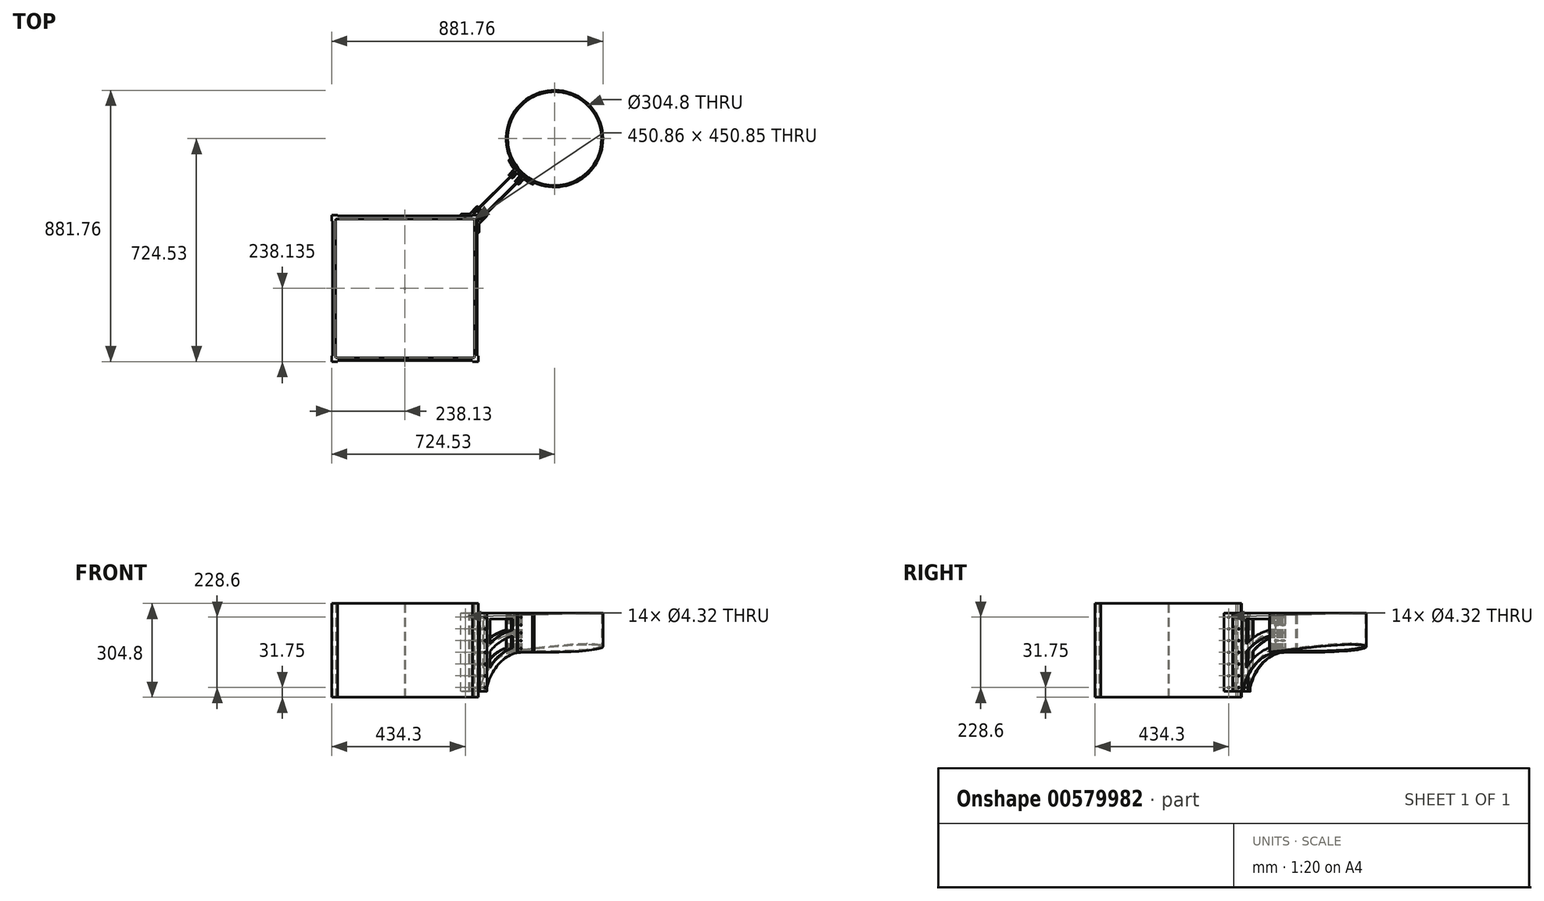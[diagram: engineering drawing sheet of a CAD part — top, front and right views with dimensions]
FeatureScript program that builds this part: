
annotation { "Feature Type Name" : "Feature", "Feature Type Description" : "" }
export const myFeature = defineFeature(function(context is Context, id is Id, definition is map)
    precondition{}
    {
        {
            var Q0;
            Q0=qCreatedBy(makeId("Top.planeOp"),FACE);
            var sketch = newSketch(context, id + "F0", { "sketchPlane" : qUnion([Q0])});
            skLineSegment(sketch, "E0.bottom", {"start": v(234.95, -234.95) * mm, "end": v(-234.95, -234.95) * mm});
            skLineSegment(sketch, "E0.top", {"start": v(234.95, 234.95) * mm, "end": v(-234.95, 234.95) * mm});
            skLineSegment(sketch, "E0.left", {"start": v(234.95, -234.95) * mm, "end": v(234.95, 234.95) * mm});
            skLineSegment(sketch, "E0.right", {"start": v(-234.95, -234.95) * mm, "end": v(-234.95, 234.95) * mm});
            skPoint(sketch, "E0.middle", {"position": v(0, 0) * mm});
            skLineSegment(sketch, "E1", {"start": v(0, 0) * mm, "end": v(234.95, 234.95) * mm});
            skLineSegment(sketch, "E2", {"start": v(234.95, 234.95) * mm, "end": v(486.4, 486.4) * mm});
            skCircle(sketch, "E3", {"center": v(486.4, 486.4) * mm, "radius": 152.4 * mm});
            skCircle(sketch, "E4", {"center": v(486.4, 486.4) * mm, "radius": 157.23 * mm});
            skLineSegment(sketch, "E5", {"start": v(-234.95, 234.95) * mm, "end": v(-234.95, 238.13) * mm});
            skLineSegment(sketch, "E6", {"start": v(-234.95, 238.13) * mm, "end": v(-238.13, 238.13) * mm});
            skLineSegment(sketch, "E7", {"start": v(-238.13, 238.13) * mm, "end": v(-238.13, 219.08) * mm});
            skLineSegment(sketch, "E8", {"start": v(-238.13, 219.08) * mm, "end": v(-234.95, 219.08) * mm});
            skLineSegment(sketch, "E9", {"start": v(-238.13, 238.13) * mm, "end": v(-219.08, 238.13) * mm});
            skLineSegment(sketch, "E10", {"start": v(-219.08, 238.13) * mm, "end": v(-219.08, 234.95) * mm});
            skLineSegment(sketch, "E11.1.0", {"start": v(-238.13, -238.13) * mm, "end": v(-219.08, -238.13) * mm});
            skLineSegment(sketch, "E11.1.1", {"start": v(-238.13, -238.13) * mm, "end": v(-238.13, -219.08) * mm});
            skLineSegment(sketch, "E11.1.2", {"start": v(-238.13, -219.08) * mm, "end": v(-234.95, -219.08) * mm});
            skLineSegment(sketch, "E11.1.3", {"start": v(-219.08, -238.13) * mm, "end": v(-219.08, -234.95) * mm});
            skLineSegment(sketch, "E11.1.4", {"start": v(-238.13, -234.95) * mm, "end": v(-238.13, -238.13) * mm});
            skLineSegment(sketch, "E11.1.5", {"start": v(-234.95, -234.95) * mm, "end": v(-238.13, -234.95) * mm});
            skLineSegment(sketch, "E11.2.0", {"start": v(238.13, -238.13) * mm, "end": v(238.13, -219.08) * mm});
            skLineSegment(sketch, "E11.2.1", {"start": v(238.13, -238.13) * mm, "end": v(219.08, -238.13) * mm});
            skLineSegment(sketch, "E11.2.2", {"start": v(219.08, -238.13) * mm, "end": v(219.08, -234.95) * mm});
            skLineSegment(sketch, "E11.2.3", {"start": v(238.13, -219.08) * mm, "end": v(234.95, -219.08) * mm});
            skLineSegment(sketch, "E11.2.4", {"start": v(234.95, -238.13) * mm, "end": v(238.13, -238.13) * mm});
            skLineSegment(sketch, "E11.2.5", {"start": v(234.95, -234.95) * mm, "end": v(234.95, -238.13) * mm});
            skLineSegment(sketch, "E11.3.0", {"start": v(238.13, 238.13) * mm, "end": v(219.08, 238.13) * mm});
            skLineSegment(sketch, "E11.3.1", {"start": v(238.13, 238.13) * mm, "end": v(238.13, 219.08) * mm});
            skLineSegment(sketch, "E11.3.2", {"start": v(238.13, 219.08) * mm, "end": v(234.95, 219.08) * mm});
            skLineSegment(sketch, "E11.3.3", {"start": v(219.08, 238.13) * mm, "end": v(219.08, 234.95) * mm});
            skLineSegment(sketch, "E11.3.4", {"start": v(238.13, 234.95) * mm, "end": v(238.13, 238.13) * mm});
            skLineSegment(sketch, "E11.3.5", {"start": v(234.95, 234.95) * mm, "end": v(238.13, 234.95) * mm});
            skLineSegment(sketch, "E12.0", {"start": v(-225.42, -225.42) * mm, "end": v(-225.43, 225.43) * mm});
            skLineSegment(sketch, "E12.1", {"start": v(225.43, -225.42) * mm, "end": v(-225.42, -225.42) * mm});
            skLineSegment(sketch, "E12.2", {"start": v(225.43, -225.42) * mm, "end": v(225.42, 225.43) * mm});
            skLineSegment(sketch, "E12.3", {"start": v(225.42, 225.43) * mm, "end": v(-225.43, 225.43) * mm});
            skSolve(sketch);
        }
        {
            var Q0;
            Q0=makeQuery(id+"F0.imprint","IMPRINT",FACE,{"disambiguationData":[TD([[makeQuery(id+"F0.imprint","IMPRINT",EDGE,{"derivedFrom":sQuery(id+"F0.wireOp",EDGE,"E3")}),-1.0]])]});
            extrude(context, id + "F1", {"entities" : qUnion([Q0]), "depth" : 304.8 * mm, "offsetDistance" : 25.4 * mm});
        }
        {
            var Q0;
            Q0=makeQuery(id+"F0.imprint","IMPRINT",FACE,{"disambiguationData":[TD([[makeQuery(id+"F0.imprint","IMPRINT",EDGE,{"derivedFrom":sQuery(id+"F0.wireOp",EDGE,"E12.0")}),1.0]])]});
            var Q1;
            Q1=makeQuery(id+"F0.imprint","IMPRINT",FACE,{"disambiguationData":[TD([[makeQuery(id+"F0.imprint","IMPRINT",EDGE,{"derivedFrom":sQuery(id+"F0.wireOp",EDGE,"E11.3.1")}),-1.0]])]});
            var Q2;
            {var subQ4=sQuery(id+"F0.wireOp",EDGE,"E11.3.0");Q2=makeQuery(id+"F0.imprint","IMPRINT",FACE,{"disambiguationData":[TD([[makeQuery(id+"F0.imprint","IMPRINT",EDGE,{"derivedFrom":subQ4}),1.0]])]});}
            var Q3;
            Q3=makeQuery(id+"F0.imprint","IMPRINT",FACE,{"disambiguationData":[TD([[makeQuery(id+"F0.imprint","IMPRINT",EDGE,{"derivedFrom":sQuery(id+"F0.wireOp",EDGE,"E11.2.0")}),1.0]])]});
            var Q4;
            {var subQ1=sQuery(id+"F0.wireOp",EDGE,"E5");Q4=makeQuery(id+"F0.imprint","IMPRINT",FACE,{"disambiguationData":[TD([[makeQuery(id+"F0.imprint","IMPRINT",EDGE,{"derivedFrom":subQ1}),1.0]])]});}
            var Q5;
            Q5=makeQuery(id+"F0.imprint","IMPRINT",FACE,{"disambiguationData":[TD([[makeQuery(id+"F0.imprint","IMPRINT",EDGE,{"derivedFrom":sQuery(id+"F0.wireOp",EDGE,"E11.2.1")}),-1.0]])]});
            var Q6;
            {var subQ0=sQuery(id+"F0.wireOp",EDGE,"E5");Q6=makeQuery(id+"F0.imprint","IMPRINT",FACE,{"disambiguationData":[TD([[makeQuery(id+"F0.imprint","IMPRINT",EDGE,{"derivedFrom":subQ0}),-1.0]])]});}
            var Q7;
            Q7=makeQuery(id+"F0.imprint","IMPRINT",FACE,{"disambiguationData":[TD([[makeQuery(id+"F0.imprint","IMPRINT",EDGE,{"derivedFrom":sQuery(id+"F0.wireOp",EDGE,"E11.1.0")}),1.0]])]});
            var Q8;
            Q8=makeQuery(id+"F0.imprint","IMPRINT",FACE,{"disambiguationData":[TD([[makeQuery(id+"F0.imprint","IMPRINT",EDGE,{"derivedFrom":sQuery(id+"F0.wireOp",EDGE,"E11.1.1")}),-1.0]])]});
            var Q9;
            {var subQ2=sQuery(id+"F0.wireOp",EDGE,"E11.3.4");Q9=makeQuery(id+"F0.imprint","IMPRINT",FACE,{"disambiguationData":[TD([[makeQuery(id+"F0.imprint","IMPRINT",EDGE,{"derivedFrom":subQ2}),1.0]])]});}
            extrude(context, id + "F2", {"entities" : qUnion([Q0, Q1, Q2, Q3, Q4, Q5, Q6, Q7, Q8, Q9]), "depth" : 304.8 * mm, "offsetDistance" : 25.4 * mm});
        }
        {
            var Q0;
            Q0=makeQuery(id+"F1.opExtrude","CAP_FACE",FACE,{"disambiguationData":[OSD([sQuery(id+"F0.wireOp",EDGE,"E3"),sQuery(id+"F0.wireOp",EDGE,"E4")])],"isStart":false});
            var sketch = newSketch(context, id + "F3", { "sketchPlane" : qUnion([Q0])});
            skCircle(sketch, "E13", {"center": v(486.4, 486.4) * mm, "radius": 157.23 * mm});
            skArc(sketch, "E14", {"start": v(366.99, 372.3) * mm, "mid": v(369.6, 369.6) * mm, "end": v(372.3, 366.99) * mm});
            skLineSegment(sketch, "E15", {"start": v(486.4, 486.4) * mm, "end": v(643.62, 486.4) * mm});
            skLineSegment(sketch, "E16", {"start": v(643.62, 486.4) * mm, "end": v(645.21, 486.4) * mm});
            skCircle(sketch, "E17", {"center": v(486.4, 486.4) * mm, "radius": 158.81 * mm});
            skLineSegment(sketch, "E18", {"start": v(369.6, 369.6) * mm, "end": v(244.47, 244.48) * mm});
            skLineSegment(sketch, "E19", {"start": v(486.4, 486.4) * mm, "end": v(477.42, 495.38) * mm});
            skLineSegment(sketch, "E20", {"start": v(360.97, 378.93) * mm, "end": v(345.53, 363.49) * mm});
            skLineSegment(sketch, "E21", {"start": v(477.42, 495.38) * mm, "end": v(475.17, 497.62) * mm});
            skLineSegment(sketch, "E22", {"start": v(358.92, 381.37) * mm, "end": v(343.28, 365.73) * mm});
            skLineSegment(sketch, "E23", {"start": v(645.21, 486.4) * mm, "end": v(651.56, 486.4) * mm});
            skLineSegment(sketch, "E24", {"start": v(238.13, 238.13) * mm, "end": v(219.08, 238.13) * mm});
            skLineSegment(sketch, "E25", {"start": v(219.08, 238.13) * mm, "end": v(219.08, 234.95) * mm});
            skLineSegment(sketch, "E26", {"start": v(219.08, 234.95) * mm, "end": v(180.98, 234.95) * mm});
            skLineSegment(sketch, "E27", {"start": v(180.98, 234.95) * mm, "end": v(180.98, 238.76) * mm});
            skLineSegment(sketch, "E28", {"start": v(475.17, 497.62) * mm, "end": v(470.68, 502.11) * mm});
            skLineSegment(sketch, "E29", {"start": v(353.4, 384.83) * mm, "end": v(338.8, 370.22) * mm});
            skLineSegment(sketch, "E30", {"start": v(477.42, 495.38) * mm, "end": v(481.9, 490.89) * mm});
            skLineSegment(sketch, "E31", {"start": v(363.35, 372.33) * mm, "end": v(350.02, 359) * mm});
            skLineSegment(sketch, "E32", {"start": v(353.4, 384.83) * mm, "end": v(337, 368.43) * mm});
            skLineSegment(sketch, "E33", {"start": v(338.8, 366.63) * mm, "end": v(339.69, 365.73) * mm});
            skArc(sketch, "E34.trimOffspring", {"start": v(358.92, 381.37) * mm, "mid": v(359.94, 380.15) * mm, "end": v(360.97, 378.93) * mm});
            skLineSegment(sketch, "E35.trimOffspring", {"start": v(345.53, 359.9) * mm, "end": v(346.42, 359) * mm});
            skLineSegment(sketch, "E36", {"start": v(235.5, 244.48) * mm, "end": v(245.3, 254.29) * mm});
            skLineSegment(sketch, "E37", {"start": v(245.3, 257.88) * mm, "end": v(244.41, 258.78) * mm});
            skLineSegment(sketch, "E38.trimOffspring", {"start": v(234.08, 265.51) * mm, "end": v(210.61, 242.04) * mm});
            skLineSegment(sketch, "E39.trimOffspring", {"start": v(247.1, 256.09) * mm, "end": v(235.5, 244.47) * mm});
            skLineSegment(sketch, "E40", {"start": v(183.52, 241.3) * mm, "end": v(208.82, 241.3) * mm});
            skLineSegment(sketch, "E41", {"start": v(238.13, 244.48) * mm, "end": v(235.5, 244.48) * mm});
            skLineSegment(sketch, "E42", {"start": v(223.34, 241.3) * mm, "end": v(221.1, 243.55) * mm});
            skLineSegment(sketch, "E43.trimOffspring", {"start": v(238.57, 264.62) * mm, "end": v(237.68, 265.51) * mm});
            skLineSegment(sketch, "E44", {"start": v(486.4, 486.4) * mm, "end": v(339.03, 417.68) * mm});
            skPoint(sketch, "E45.visualSharp", {"position": v(354.96, 386.39) * mm});
            skArc(sketch, "E45.filletArc", {"start": v(353.4, 384.83) * mm, "mid": v(354.13, 386.44) * mm, "end": v(353.64, 388.14) * mm});
            skPoint(sketch, "E46.visualSharp", {"position": v(337, 368.43) * mm});
            skArc(sketch, "E46.filletArc", {"start": v(338.8, 370.22) * mm, "mid": v(338.05, 368.43) * mm, "end": v(338.8, 366.63) * mm});
            skPoint(sketch, "E47.visualSharp", {"position": v(348.22, 357.2) * mm});
            skArc(sketch, "E47.filletArc", {"start": v(346.42, 359) * mm, "mid": v(348.22, 358.25) * mm, "end": v(350.02, 359) * mm});
            skPoint(sketch, "E48.visualSharp", {"position": v(365.2, 374.19) * mm});
            skArc(sketch, "E48.filletArc", {"start": v(366.99, 372.3) * mm, "mid": v(365.18, 373.08) * mm, "end": v(363.35, 372.33) * mm});
            skPoint(sketch, "E49.visualSharp", {"position": v(235.88, 267.31) * mm});
            skArc(sketch, "E49.filletArc", {"start": v(237.68, 265.51) * mm, "mid": v(235.88, 266.26) * mm, "end": v(234.08, 265.51) * mm});
            skPoint(sketch, "E50.visualSharp", {"position": v(247.1, 256.09) * mm});
            skArc(sketch, "E50.filletArc", {"start": v(245.3, 254.29) * mm, "mid": v(246.05, 256.09) * mm, "end": v(245.3, 257.88) * mm});
            skPoint(sketch, "E51.visualSharp", {"position": v(209.87, 241.3) * mm});
            skArc(sketch, "E51.filletArc", {"start": v(208.82, 241.3) * mm, "mid": v(209.79, 241.5) * mm, "end": v(210.61, 242.04) * mm});
            skPoint(sketch, "E52.visualSharp", {"position": v(180.98, 241.3) * mm});
            skArc(sketch, "E52.filletArc", {"start": v(183.52, 241.3) * mm, "mid": v(181.72, 240.56) * mm, "end": v(180.98, 238.76) * mm});
            skLineSegment(sketch, "E53.trimOffspring", {"start": v(238.57, 261.02) * mm, "end": v(221.1, 243.55) * mm});
            skLineSegment(sketch, "E54.trimOffspring", {"start": v(240.82, 258.78) * mm, "end": v(223.34, 241.3) * mm});
            skPoint(sketch, "E55.visualSharp", {"position": v(341.49, 363.94) * mm});
            skArc(sketch, "E55.filletArc", {"start": v(339.69, 365.73) * mm, "mid": v(341.49, 364.99) * mm, "end": v(343.28, 365.73) * mm});
            skPoint(sketch, "E56.visualSharp", {"position": v(343.73, 361.7) * mm});
            skArc(sketch, "E56.filletArc", {"start": v(345.53, 363.49) * mm, "mid": v(344.78, 361.7) * mm, "end": v(345.53, 359.9) * mm});
            skPoint(sketch, "E57.visualSharp", {"position": v(240.37, 262.82) * mm});
            skArc(sketch, "E57.filletArc", {"start": v(238.57, 261.02) * mm, "mid": v(239.32, 262.82) * mm, "end": v(238.57, 264.62) * mm});
            skPoint(sketch, "E58.visualSharp", {"position": v(242.62, 260.58) * mm});
            skArc(sketch, "E58.filletArc", {"start": v(244.41, 258.78) * mm, "mid": v(242.62, 259.52) * mm, "end": v(240.82, 258.78) * mm});
            skLineSegment(sketch, "E59.MirrorCS", {"start": v(359.9, 345.53) * mm, "end": v(359, 346.42) * mm});
            skArc(sketch, "E60.MirrorCS", {"start": v(363.49, 345.53) * mm, "mid": v(361.7, 344.78) * mm, "end": v(359.9, 345.53) * mm});
            skLineSegment(sketch, "E61.MirrorCS", {"start": v(366.63, 338.8) * mm, "end": v(365.73, 339.69) * mm});
            skArc(sketch, "E62.MirrorCS", {"start": v(372.3, 366.99) * mm, "mid": v(373.08, 365.18) * mm, "end": v(372.33, 363.35) * mm});
            skArc(sketch, "E63.MirrorCS", {"start": v(384.83, 353.4) * mm, "mid": v(386.44, 354.13) * mm, "end": v(388.14, 353.64) * mm});
            skArc(sketch, "E64.MirrorCS", {"start": v(359, 346.42) * mm, "mid": v(358.25, 348.22) * mm, "end": v(359, 350.02) * mm});
            skArc(sketch, "E65.MirrorCS", {"start": v(365.73, 339.69) * mm, "mid": v(364.99, 341.49) * mm, "end": v(365.73, 343.28) * mm});
            skArc(sketch, "E66.MirrorCS", {"start": v(370.22, 338.8) * mm, "mid": v(368.43, 338.05) * mm, "end": v(366.63, 338.8) * mm});
            skArc(sketch, "E67.MirrorCS", {"start": v(381.37, 358.92) * mm, "mid": v(380.15, 359.94) * mm, "end": v(378.93, 360.97) * mm});
            skLineSegment(sketch, "E68.MirrorCS", {"start": v(384.83, 353.4) * mm, "end": v(368.43, 337) * mm});
            skPoint(sketch, "E69.MirrorP", {"position": v(386.39, 354.96) * mm});
            skPoint(sketch, "E70.MirrorP", {"position": v(363.94, 341.49) * mm});
            skPoint(sketch, "E71.MirrorP", {"position": v(368.43, 337) * mm});
            skPoint(sketch, "E72.MirrorP", {"position": v(361.7, 343.73) * mm});
            skPoint(sketch, "E73.MirrorP", {"position": v(374.19, 365.2) * mm});
            skPoint(sketch, "E74.MirrorP", {"position": v(357.2, 348.22) * mm});
            skLineSegment(sketch, "E75.MirrorCS", {"start": v(381.37, 358.92) * mm, "end": v(365.73, 343.28) * mm});
            skLineSegment(sketch, "E76.MirrorCS", {"start": v(372.33, 363.35) * mm, "end": v(359, 350.02) * mm});
            skLineSegment(sketch, "E77.MirrorCS", {"start": v(378.93, 360.97) * mm, "end": v(363.49, 345.53) * mm});
            skLineSegment(sketch, "E78.MirrorCS", {"start": v(384.83, 353.4) * mm, "end": v(370.22, 338.8) * mm});
            skLineSegment(sketch, "E79.MirrorCS", {"start": v(486.4, 486.4) * mm, "end": v(417.68, 339.03) * mm});
            skLineSegment(sketch, "E80.MirrorCS", {"start": v(238.13, 219.08) * mm, "end": v(234.95, 219.08) * mm});
            skArc(sketch, "E81.MirrorCS", {"start": v(258.78, 244.41) * mm, "mid": v(259.52, 242.62) * mm, "end": v(258.78, 240.82) * mm});
            skArc(sketch, "E82.MirrorCS", {"start": v(265.51, 237.68) * mm, "mid": v(266.26, 235.88) * mm, "end": v(265.51, 234.08) * mm});
            skArc(sketch, "E83.MirrorCS", {"start": v(254.29, 245.3) * mm, "mid": v(256.09, 246.05) * mm, "end": v(257.88, 245.3) * mm});
            skLineSegment(sketch, "E84.MirrorCS", {"start": v(264.62, 238.57) * mm, "end": v(265.51, 237.68) * mm});
            skArc(sketch, "E85.MirrorCS", {"start": v(241.3, 208.82) * mm, "mid": v(241.5, 209.79) * mm, "end": v(242.04, 210.61) * mm});
            skLineSegment(sketch, "E86.MirrorCS", {"start": v(244.47, 238.13) * mm, "end": v(244.47, 235.5) * mm});
            skArc(sketch, "E87.MirrorCS", {"start": v(261.02, 238.57) * mm, "mid": v(262.82, 239.32) * mm, "end": v(264.62, 238.57) * mm});
            skArc(sketch, "E88.MirrorCS", {"start": v(241.3, 183.52) * mm, "mid": v(240.56, 181.72) * mm, "end": v(238.76, 180.98) * mm});
            skLineSegment(sketch, "E89.MirrorCS", {"start": v(257.88, 245.3) * mm, "end": v(258.78, 244.41) * mm});
            skLineSegment(sketch, "E90.MirrorCS", {"start": v(241.3, 223.34) * mm, "end": v(243.55, 221.1) * mm});
            skLineSegment(sketch, "E91.MirrorCS", {"start": v(234.95, 180.98) * mm, "end": v(238.76, 180.98) * mm});
            skLineSegment(sketch, "E92.MirrorCS", {"start": v(244.47, 235.5) * mm, "end": v(254.29, 245.3) * mm});
            skLineSegment(sketch, "E93.MirrorCS", {"start": v(238.13, 238.13) * mm, "end": v(238.13, 219.08) * mm});
            skPoint(sketch, "E94.MirrorP", {"position": v(256.09, 247.1) * mm});
            skPoint(sketch, "E95.MirrorP", {"position": v(262.82, 240.37) * mm});
            skPoint(sketch, "E96.MirrorP", {"position": v(241.3, 209.87) * mm});
            skLineSegment(sketch, "E97.MirrorCS", {"start": v(265.51, 234.08) * mm, "end": v(242.04, 210.61) * mm});
            skPoint(sketch, "E98.MirrorP", {"position": v(260.58, 242.62) * mm});
            skLineSegment(sketch, "E99.MirrorCS", {"start": v(261.02, 238.57) * mm, "end": v(243.55, 221.1) * mm});
            skPoint(sketch, "E100.MirrorP", {"position": v(267.31, 235.88) * mm});
            skLineSegment(sketch, "E101.MirrorCS", {"start": v(258.78, 240.82) * mm, "end": v(241.3, 223.34) * mm});
            skPoint(sketch, "E102.MirrorP", {"position": v(241.3, 180.98) * mm});
            skLineSegment(sketch, "E103.MirrorCS", {"start": v(241.3, 183.52) * mm, "end": v(241.3, 208.82) * mm});
            skLineSegment(sketch, "E104.MirrorCS", {"start": v(256.09, 247.1) * mm, "end": v(244.47, 235.5) * mm});
            skLineSegment(sketch, "E105.MirrorCS", {"start": v(234.95, 219.08) * mm, "end": v(234.95, 180.98) * mm});
            skLineSegment(sketch, "E106", {"start": v(238.13, 244.48) * mm, "end": v(241.94, 244.48) * mm});
            skLineSegment(sketch, "E107", {"start": v(244.47, 241.94) * mm, "end": v(244.47, 238.13) * mm});
            skPoint(sketch, "E108.MirrorCS.start.orphan", {"position": v(238.12, 238.13) * mm});
            skPoint(sketch, "E109.visualSharp", {"position": v(244.47, 244.48) * mm});
            skArc(sketch, "E109.filletArc", {"start": v(244.47, 241.94) * mm, "mid": v(243.73, 243.73) * mm, "end": v(241.94, 244.48) * mm});
            skLineSegment(sketch, "E110.0", {"start": v(216.54, 238.13) * mm, "end": v(216.54, 234.95) * mm});
            skLineSegment(sketch, "E111.0", {"start": v(238.13, 216.53) * mm, "end": v(234.95, 216.53) * mm});
            skLineSegment(sketch, "E112", {"start": v(219.08, 238.13) * mm, "end": v(216.54, 238.13) * mm});
            skLineSegment(sketch, "E113", {"start": v(238.13, 216.53) * mm, "end": v(238.13, 219.08) * mm});
            skArc(sketch, "E114.trimOffspring", {"start": v(378.93, 360.97) * mm, "mid": v(380.15, 359.94) * mm, "end": v(381.37, 358.92) * mm});
            skArc(sketch, "E115.trimOffspring", {"start": v(388.14, 353.64) * mm, "mid": v(400.83, 345.12) * mm, "end": v(414.27, 337.82) * mm});
            skArc(sketch, "E116.trimOffspring", {"start": v(337.82, 414.27) * mm, "mid": v(345.12, 400.83) * mm, "end": v(353.64, 388.14) * mm});
            skPoint(sketch, "E117.visualSharp", {"position": v(336.7, 416.6) * mm});
            skArc(sketch, "E117.filletArc", {"start": v(339.03, 417.68) * mm, "mid": v(337.7, 416.23) * mm, "end": v(337.82, 414.27) * mm});
            skPoint(sketch, "E118.visualSharp", {"position": v(416.6, 336.7) * mm});
            skArc(sketch, "E118.filletArc", {"start": v(414.27, 337.82) * mm, "mid": v(416.23, 337.7) * mm, "end": v(417.68, 339.03) * mm});
            skSolve(sketch);
        }
        {
            var Q0;
            Q0=makeQuery(id+"F3.imprint","IMPRINT",FACE,{"disambiguationData":[TD([[makeQuery(id+"F3.imprint","IMPRINT",EDGE,{"derivedFrom":sQuery(id+"F3.wireOp",EDGE,"E20")}),1.0]])]});
            var Q1;
            Q1=makeQuery(id+"F3.imprint","IMPRINT",FACE,{"disambiguationData":[TD([[makeQuery(id+"F3.imprint","IMPRINT",EDGE,{"derivedFrom":sQuery(id+"F3.wireOp",EDGE,"E24")}),-1.0]])]});
            extrude(context, id + "F4", {"entities" : qUnion([Q0, Q1]), "oppositeDirection" : true, "depth" : 254 * mm, "offsetDistance" : 25.4 * mm});
        }
        {
            var Q0;
            Q0=makeQuery(id+"F4.opExtrude","SWEPT_FACE",FACE,{"disambiguationData":[OSD([sQuery(id+"F3.wireOp",EDGE,"E97.MirrorCS")])]});
            var sketch = newSketch(context, id + "F5", { "sketchPlane" : qUnion([Q0])});
            skLineSegment(sketch, "E119", {"start": v(538.63, 304.8) * mm, "end": v(538.63, 177.8) * mm});
            skLineSegment(sketch, "E120", {"start": v(538.63, 177.8) * mm, "end": v(487.83, 177.8) * mm});
            skLineSegment(sketch, "E121", {"start": v(487.83, 177.8) * mm, "end": v(487.83, -25.4) * mm});
            skLineSegment(sketch, "E122", {"start": v(487.83, -25.4) * mm, "end": v(564.03, -25.4) * mm});
            skLineSegment(sketch, "E123", {"start": v(564.03, -25.4) * mm, "end": v(564.03, 177.8) * mm});
            skLineSegment(sketch, "E124", {"start": v(564.03, 177.8) * mm, "end": v(538.63, 177.8) * mm});
            skSolve(sketch);
        }
        {
            var Q0;
            Q0=makeQuery(id+"F5.imprint","IMPRINT",FACE,{"disambiguationData":[TD([[makeQuery(id+"F5.imprint","IMPRINT",EDGE,{"derivedFrom":sQuery(id+"F5.wireOp",EDGE,"E120")}),1.0]])]});
            extrude(context, id + "F6", {"entities" : qUnion([Q0]), "operationType" : NewBodyOperationType.REMOVE, "endBound" : BoundingType.SYMMETRIC, "oppositeDirection" : true, "depth" : 254 * mm, "offsetDistance" : 25.4 * mm});
        }
        {
            var Q0;
            Q0=makeQuery(id+"F4.opExtrude","SWEPT_FACE",FACE,{"disambiguationData":[OSD([sQuery(id+"F3.wireOp",EDGE,"E42")])]});
            var Q1;
            Q1=makeQuery(id+"F4.opExtrude","SWEPT_FACE",FACE,{"disambiguationData":[OSD([sQuery(id+"F3.wireOp",EDGE,"E90.MirrorCS")])]});
            extrude(context, id + "F7", {"entities" : qUnion([Q0, Q1]), "depth" : 194.3 * mm, "offsetDistance" : 25.4 * mm});
        }
        {
            var Q0;
            Q0=makeQuery(id+"F7.opExtrude","SWEPT_FACE",FACE,{"disambiguationData":[OSD([sQuery(id+"F3.wireOp",EDGE,"E90.MirrorCS"),sQuery(id+"F3.wireOp",EDGE,"E99.MirrorCS")])]});
            var sketch = newSketch(context, id + "F8", { "sketchPlane" : qUnion([Q0])});
            skLineSegment(sketch, "E125", {"start": v(355.8, 50.8) * mm, "end": v(355.8, 37.36) * mm});
            skLineSegment(sketch, "E126", {"start": v(522.86, 177.8) * mm, "end": v(532.9, 177.8) * mm});
            skArc(sketch, "E127", {"start": v(522.86, 177.8) * mm, "mid": v(417.94, 142.44) * mm, "end": v(355.8, 50.8) * mm});
            skLineSegment(sketch, "E128", {"start": v(355.8, 37.36) * mm, "end": v(550.78, 37.36) * mm});
            skLineSegment(sketch, "E129", {"start": v(532.9, 177.8) * mm, "end": v(532.9, 37.36) * mm});
            skSolve(sketch);
        }
        {
            var Q0;
            Q0=qSketchRegion(id+"F8",true);
            extrude(context, id + "F9", {"entities" : qUnion([Q0]), "operationType" : NewBodyOperationType.REMOVE, "oppositeDirection" : true, "depth" : 127 * mm, "offsetDistance" : 25.4 * mm});
        }
        {
            var Q0;
            {var subQ0=sQuery(id+"F3.wireOp",EDGE,"E44");var subQ1=sQuery(id+"F3.wireOp",EDGE,"E13");var subQ2=makeQuery(id+"F3.imprint","INTERSECT",VERTEX,{"derivedFrom":[subQ1,subQ0]});Q0=makeQuery(id+"F3.imprint","IMPRINT",FACE,{"disambiguationData":[TD([[makeQuery(id+"F3.imprint","IMPRINT",EDGE,{"disambiguationData":[TD([[subQ2,-1.0]])],"derivedFrom":subQ1}),-1.0]])]});}
            extrude(context, id + "F10", {"entities" : qUnion([Q0]), "oppositeDirection" : true, "depth" : 127 * mm, "offsetDistance" : 25.4 * mm});
        }
        {
            var Q0;
            Q0=sQuery(id+"F3.wireOp",EDGE,"E18");
            cPlane(context, id + "F11", {"entities" : qUnion([Q0]), "cplaneType" : CPlaneType.LINE_ANGLE, "offset" : 25.4 * mm, "angle" : 90 * degree, "width" : 152.4 * mm, "height" : 152.4 * mm});
        }
        {
            var Q0;
            Q0=qCreatedBy(id+"F11.planeOp",FACE);
            var sketch = newSketch(context, id + "F12", { "sketchPlane" : qUnion([Q0])});
            skLineSegment(sketch, "E130", {"start": v(521.3, 304.8) * mm, "end": v(521.3, 275.68) * mm});
            skLineSegment(sketch, "E131", {"start": v(521.3, 304.8) * mm, "end": v(687.87, 304.8) * mm});
            skLineSegment(sketch, "E132", {"start": v(687.87, 304.8) * mm, "end": v(530.64, 304.8) * mm});
            skLineSegment(sketch, "E133", {"start": v(530.64, 304.8) * mm, "end": v(530.64, 177.8) * mm});
            skLineSegment(sketch, "E134", {"start": v(687.87, 304.8) * mm, "end": v(845.1, 304.8) * mm});
            skLineSegment(sketch, "E135", {"start": v(845.1, 304.8) * mm, "end": v(845.1, 203.2) * mm});
            skLineSegment(sketch, "E136", {"start": v(530.64, 177.8) * mm, "end": v(526.36, 177.8) * mm});
            skArc(sketch, "E137", {"start": v(530.64, 177.8) * mm, "mid": v(688.38, 184.16) * mm, "end": v(845.1, 203.2) * mm});
            skLineSegment(sketch, "E138", {"start": v(845.1, 203.2) * mm, "end": v(870.5, 203.2) * mm});
            skLineSegment(sketch, "E139", {"start": v(870.5, 203.2) * mm, "end": v(870.5, -50.8) * mm});
            skLineSegment(sketch, "E140", {"start": v(870.5, -50.8) * mm, "end": v(526.36, -50.8) * mm});
            skLineSegment(sketch, "E141", {"start": v(526.36, 177.8) * mm, "end": v(526.36, -50.8) * mm});
            skSolve(sketch);
        }
        {
            var Q0;
            Q0=makeQuery(id+"F12.imprint","IMPRINT",FACE,{"disambiguationData":[TD([[makeQuery(id+"F12.imprint","IMPRINT",EDGE,{"derivedFrom":sQuery(id+"F12.wireOp",EDGE,"E136")}),1.0]])]});
            extrude(context, id + "F13", {"entities" : qUnion([Q0]), "operationType" : NewBodyOperationType.REMOVE, "endBound" : BoundingType.SYMMETRIC, "oppositeDirection" : true, "depth" : 381 * mm, "offsetDistance" : 25.4 * mm});
        }
        {
            var Q0;
            Q0=qCreatedBy(makeId("Top.planeOp"),FACE);
            var sketch = newSketch(context, id + "F14", { "sketchPlane" : qUnion([Q0])});
            skCircle(sketch, "E142", {"center": v(0, 0) * mm, "radius": 1.27 * mm});
            skSolve(sketch);
        }
        {
            var Q0;
            Q0=qSketchRegion(id+"F14",true);
            extrude(context, id + "F15", {"entities" : qUnion([Q0]), "depth" : 304.8 * mm, "offsetDistance" : 25.4 * mm});
        }
        {
            var Q0;
            Q0=makeQuery(id+"F1.opExtrude","SWEPT_FACE",FACE,{"disambiguationData":[OSD([sQuery(id+"F0.wireOp",EDGE,"E3")])]});
            fillet(context, id + "F16", {"entities" : qUnion([Q0]), "radius" : 3.8 * mm, "tangentPropagation" : true, "allowEdgeOverflow" : false});
        }
        {
            var Q0;
            Q0=makeQuery(id+"F1.opExtrude","SWEPT_BODY",BODY,{"disambiguationData":[OSD([sQuery(id+"F0.wireOp",EDGE,"E3"),sQuery(id+"F0.wireOp",EDGE,"E4")])]});
            var Q1;
            Q1=makeQuery(id+"F4.opExtrude","SWEPT_BODY",BODY,{"disambiguationData":[OSD([sQuery(id+"F3.wireOp",EDGE,"E14"),sQuery(id+"F3.wireOp",EDGE,"E17"),sQuery(id+"F3.wireOp",EDGE,"E20"),sQuery(id+"F3.wireOp",EDGE,"E22"),sQuery(id+"F3.wireOp",EDGE,"E31"),sQuery(id+"F3.wireOp",EDGE,"E32"),sQuery(id+"F3.wireOp",EDGE,"E33"),sQuery(id+"F3.wireOp",EDGE,"E34.trimOffspring"),sQuery(id+"F3.wireOp",EDGE,"E35.trimOffspring"),sQuery(id+"F3.wireOp",EDGE,"E44"),sQuery(id+"F3.wireOp",EDGE,"E45.filletArc"),sQuery(id+"F3.wireOp",EDGE,"E46.filletArc"),sQuery(id+"F3.wireOp",EDGE,"E47.filletArc"),sQuery(id+"F3.wireOp",EDGE,"E48.filletArc"),sQuery(id+"F3.wireOp",EDGE,"E55.filletArc"),sQuery(id+"F3.wireOp",EDGE,"E56.filletArc"),sQuery(id+"F3.wireOp",EDGE,"E59.MirrorCS"),sQuery(id+"F3.wireOp",EDGE,"E60.MirrorCS"),sQuery(id+"F3.wireOp",EDGE,"E61.MirrorCS"),sQuery(id+"F3.wireOp",EDGE,"E62.MirrorCS"),sQuery(id+"F3.wireOp",EDGE,"E63.MirrorCS"),sQuery(id+"F3.wireOp",EDGE,"E64.MirrorCS"),sQuery(id+"F3.wireOp",EDGE,"E65.MirrorCS"),sQuery(id+"F3.wireOp",EDGE,"E66.MirrorCS"),sQuery(id+"F3.wireOp",EDGE,"E75.MirrorCS"),sQuery(id+"F3.wireOp",EDGE,"E76.MirrorCS"),sQuery(id+"F3.wireOp",EDGE,"E77.MirrorCS"),sQuery(id+"F3.wireOp",EDGE,"E78.MirrorCS"),sQuery(id+"F3.wireOp",EDGE,"E79.MirrorCS"),sQuery(id+"F3.wireOp",EDGE,"E114.trimOffspring"),sQuery(id+"F3.wireOp",EDGE,"E115.trimOffspring"),sQuery(id+"F3.wireOp",EDGE,"E116.trimOffspring"),sQuery(id+"F3.wireOp",EDGE,"E117.filletArc"),sQuery(id+"F3.wireOp",EDGE,"E118.filletArc")])]});
            var Q2;
            Q2=makeQuery(id+"F4.opExtrude","SWEPT_BODY",BODY,{"disambiguationData":[OSD([sQuery(id+"F3.wireOp",EDGE,"E24"),sQuery(id+"F3.wireOp",EDGE,"E26"),sQuery(id+"F3.wireOp",EDGE,"E27"),sQuery(id+"F3.wireOp",EDGE,"E37"),sQuery(id+"F3.wireOp",EDGE,"E38.trimOffspring"),sQuery(id+"F3.wireOp",EDGE,"E39.trimOffspring"),sQuery(id+"F3.wireOp",EDGE,"E40"),sQuery(id+"F3.wireOp",EDGE,"E41"),sQuery(id+"F3.wireOp",EDGE,"E42"),sQuery(id+"F3.wireOp",EDGE,"E43.trimOffspring"),sQuery(id+"F3.wireOp",EDGE,"E49.filletArc"),sQuery(id+"F3.wireOp",EDGE,"E50.filletArc"),sQuery(id+"F3.wireOp",EDGE,"E51.filletArc"),sQuery(id+"F3.wireOp",EDGE,"E52.filletArc"),sQuery(id+"F3.wireOp",EDGE,"E53.trimOffspring"),sQuery(id+"F3.wireOp",EDGE,"E54.trimOffspring"),sQuery(id+"F3.wireOp",EDGE,"E57.filletArc"),sQuery(id+"F3.wireOp",EDGE,"E58.filletArc"),sQuery(id+"F3.wireOp",EDGE,"E81.MirrorCS"),sQuery(id+"F3.wireOp",EDGE,"E82.MirrorCS"),sQuery(id+"F3.wireOp",EDGE,"E83.MirrorCS"),sQuery(id+"F3.wireOp",EDGE,"E84.MirrorCS"),sQuery(id+"F3.wireOp",EDGE,"E85.MirrorCS"),sQuery(id+"F3.wireOp",EDGE,"E86.MirrorCS"),sQuery(id+"F3.wireOp",EDGE,"E87.MirrorCS"),sQuery(id+"F3.wireOp",EDGE,"E88.MirrorCS"),sQuery(id+"F3.wireOp",EDGE,"E89.MirrorCS"),sQuery(id+"F3.wireOp",EDGE,"E90.MirrorCS"),sQuery(id+"F3.wireOp",EDGE,"E91.MirrorCS"),sQuery(id+"F3.wireOp",EDGE,"E93.MirrorCS"),sQuery(id+"F3.wireOp",EDGE,"E97.MirrorCS"),sQuery(id+"F3.wireOp",EDGE,"E99.MirrorCS"),sQuery(id+"F3.wireOp",EDGE,"E101.MirrorCS"),sQuery(id+"F3.wireOp",EDGE,"E103.MirrorCS"),sQuery(id+"F3.wireOp",EDGE,"E104.MirrorCS"),sQuery(id+"F3.wireOp",EDGE,"E105.MirrorCS"),sQuery(id+"F3.wireOp",EDGE,"E106"),sQuery(id+"F3.wireOp",EDGE,"E107"),sQuery(id+"F3.wireOp",EDGE,"E109.filletArc"),sQuery(id+"F3.wireOp",EDGE,"E110.0"),sQuery(id+"F3.wireOp",EDGE,"E111.0"),sQuery(id+"F3.wireOp",EDGE,"E112"),sQuery(id+"F3.wireOp",EDGE,"E113")])]});
            var Q3;
            Q3=makeQuery(id+"F7.opExtrude","SWEPT_BODY",BODY,{"disambiguationData":[OSD([sQuery(id+"F3.wireOp",EDGE,"E42")])]});
            var Q4;
            Q4=makeQuery(id+"F7.opExtrude","SWEPT_BODY",BODY,{"disambiguationData":[OSD([sQuery(id+"F3.wireOp",EDGE,"E90.MirrorCS")])]});
            var Q5;
            Q5=makeQuery(id+"F10.opExtrude","SWEPT_BODY",BODY,{"disambiguationData":[OSD([sQuery(id+"F3.wireOp",EDGE,"E13"),sQuery(id+"F3.wireOp",EDGE,"E17"),sQuery(id+"F3.wireOp",EDGE,"E44"),sQuery(id+"F3.wireOp",EDGE,"E79.MirrorCS")])]});
            transform(context, id + "F17", {"entities" : qUnion([Q0, Q1, Q2, Q3, Q4, Q5]), "transformType" : TransformType.TRANSLATION_3D, "dx" : 0 * mm, "dy" : 0 * mm, "dz" : -31.75 * mm, "makeCopy" : false});
        }
        {
            var Q0;
            Q0=makeQuery(id+"F7.opExtrude","SWEPT_FACE",FACE,{"disambiguationData":[OSD([sQuery(id+"F3.wireOp",EDGE,"E90.MirrorCS"),sQuery(id+"F3.wireOp",EDGE,"E99.MirrorCS")])]});
            var sketch = newSketch(context, id + "F18", { "sketchPlane" : qUnion([Q0])});
            skArc(sketch, "E143.0", {"start": v(479.76, 160.21) * mm, "mid": v(422, 136.55) * mm, "end": v(374.86, 95.65) * mm});
            skLineSegment(sketch, "E144.0", {"start": v(479.76, 254) * mm, "end": v(328.55, 254) * mm});
            skLineSegment(sketch, "E145.0", {"start": v(374.86, 95.65) * mm, "end": v(374.86, 149.41) * mm});
            skLineSegment(sketch, "E146.0", {"start": v(479.76, 146.05) * mm, "end": v(479.76, 199.13) * mm});
            skArc(sketch, "E147.0", {"start": v(479.76, 199.13) * mm, "mid": v(424.13, 180.99) * mm, "end": v(374.86, 149.41) * mm});
            skArc(sketch, "E148.0", {"start": v(479.76, 218.5) * mm, "mid": v(424.71, 202.14) * mm, "end": v(374.86, 173.63) * mm});
            skLineSegment(sketch, "E149.trimOffspring", {"start": v(374.86, 173.63) * mm, "end": v(374.86, 273.05) * mm});
            skLineSegment(sketch, "E150.trimOffspring", {"start": v(479.76, 218.5) * mm, "end": v(479.76, 273.05) * mm});
            skSolve(sketch);
        }
        {
            var Q0;
            Q0=qSketchRegion(id+"F18",true);
            extrude(context, id + "F19", {"entities" : qUnion([Q0]), "operationType" : NewBodyOperationType.REMOVE, "oppositeDirection" : true, "depth" : 101.6 * mm, "offsetDistance" : 25.4 * mm});
        }
        {
            var Q0;
            Q0=makeQuery(id+"F4.opExtrude","SWEPT_FACE",FACE,{"disambiguationData":[OSD([sQuery(id+"F3.wireOp",EDGE,"E97.MirrorCS")])]});
            var sketch = newSketch(context, id + "F20", { "sketchPlane" : qUnion([Q0])});
            skLineSegment(sketch, "E151", {"start": v(320.08, 273.05) * mm, "end": v(345.48, 273.05) * mm});
            skLineSegment(sketch, "E152", {"start": v(345.48, 273.05) * mm, "end": v(345.48, 19.05) * mm});
            skLineSegment(sketch, "E153", {"start": v(345.48, 146.05) * mm, "end": v(335.48, 146.05) * mm});
            skLineSegment(sketch, "E154", {"start": v(345.48, 146.05) * mm, "end": v(345.48, 184.15) * mm});
            skLineSegment(sketch, "E155", {"start": v(345.48, 184.15) * mm, "end": v(345.48, 222.25) * mm});
            skLineSegment(sketch, "E156", {"start": v(345.48, 222.25) * mm, "end": v(345.48, 260.35) * mm});
            skLineSegment(sketch, "E157.MirrorCS", {"start": v(345.48, 146.05) * mm, "end": v(345.48, 107.95) * mm});
            skLineSegment(sketch, "E158.MirrorCS", {"start": v(345.48, 107.95) * mm, "end": v(345.48, 69.85) * mm});
            skLineSegment(sketch, "E159.MirrorCS", {"start": v(345.48, 69.85) * mm, "end": v(345.48, 31.75) * mm});
            skSolve(sketch);
        }
        {
            var Q0;
            Q0=sQuery(id+"F20.wireOp",VERTEX,"E159.MirrorCS.end");
            var Q1;
            Q1=sQuery(id+"F20.wireOp",VERTEX,"E158.MirrorCS.end");
            var Q2;
            Q2=sQuery(id+"F20.wireOp",VERTEX,"E158.MirrorCS.start");
            var Q3;
            Q3=sQuery(id+"F20.wireOp",VERTEX,"E157.MirrorCS.start");
            var Q4;
            Q4=sQuery(id+"F20.wireOp",VERTEX,"E155.start");
            var Q5;
            Q5=sQuery(id+"F20.wireOp",VERTEX,"E156.start");
            var Q6;
            Q6=sQuery(id+"F20.wireOp",VERTEX,"E156.end");
            var Q7;
            Q7=makeQuery(id+"F7.opExtrude","SWEPT_BODY",BODY,{"disambiguationData":[OSD([sQuery(id+"F3.wireOp",EDGE,"E42")])]});
            var Q8;
            Q8=makeQuery(id+"F7.opExtrude","SWEPT_BODY",BODY,{"disambiguationData":[OSD([sQuery(id+"F3.wireOp",EDGE,"E90.MirrorCS")])]});
            var Q9;
            Q9=makeQuery(id+"F4.opExtrude","SWEPT_BODY",BODY,{"disambiguationData":[OSD([sQuery(id+"F3.wireOp",EDGE,"E24"),sQuery(id+"F3.wireOp",EDGE,"E26"),sQuery(id+"F3.wireOp",EDGE,"E27"),sQuery(id+"F3.wireOp",EDGE,"E37"),sQuery(id+"F3.wireOp",EDGE,"E38.trimOffspring"),sQuery(id+"F3.wireOp",EDGE,"E39.trimOffspring"),sQuery(id+"F3.wireOp",EDGE,"E40"),sQuery(id+"F3.wireOp",EDGE,"E41"),sQuery(id+"F3.wireOp",EDGE,"E42"),sQuery(id+"F3.wireOp",EDGE,"E43.trimOffspring"),sQuery(id+"F3.wireOp",EDGE,"E49.filletArc"),sQuery(id+"F3.wireOp",EDGE,"E50.filletArc"),sQuery(id+"F3.wireOp",EDGE,"E51.filletArc"),sQuery(id+"F3.wireOp",EDGE,"E52.filletArc"),sQuery(id+"F3.wireOp",EDGE,"E53.trimOffspring"),sQuery(id+"F3.wireOp",EDGE,"E54.trimOffspring"),sQuery(id+"F3.wireOp",EDGE,"E57.filletArc"),sQuery(id+"F3.wireOp",EDGE,"E58.filletArc"),sQuery(id+"F3.wireOp",EDGE,"E81.MirrorCS"),sQuery(id+"F3.wireOp",EDGE,"E82.MirrorCS"),sQuery(id+"F3.wireOp",EDGE,"E83.MirrorCS"),sQuery(id+"F3.wireOp",EDGE,"E84.MirrorCS"),sQuery(id+"F3.wireOp",EDGE,"E85.MirrorCS"),sQuery(id+"F3.wireOp",EDGE,"E86.MirrorCS"),sQuery(id+"F3.wireOp",EDGE,"E87.MirrorCS"),sQuery(id+"F3.wireOp",EDGE,"E88.MirrorCS"),sQuery(id+"F3.wireOp",EDGE,"E89.MirrorCS"),sQuery(id+"F3.wireOp",EDGE,"E90.MirrorCS"),sQuery(id+"F3.wireOp",EDGE,"E91.MirrorCS"),sQuery(id+"F3.wireOp",EDGE,"E93.MirrorCS"),sQuery(id+"F3.wireOp",EDGE,"E97.MirrorCS"),sQuery(id+"F3.wireOp",EDGE,"E99.MirrorCS"),sQuery(id+"F3.wireOp",EDGE,"E101.MirrorCS"),sQuery(id+"F3.wireOp",EDGE,"E103.MirrorCS"),sQuery(id+"F3.wireOp",EDGE,"E104.MirrorCS"),sQuery(id+"F3.wireOp",EDGE,"E105.MirrorCS"),sQuery(id+"F3.wireOp",EDGE,"E106"),sQuery(id+"F3.wireOp",EDGE,"E107"),sQuery(id+"F3.wireOp",EDGE,"E109.filletArc"),sQuery(id+"F3.wireOp",EDGE,"E110.0"),sQuery(id+"F3.wireOp",EDGE,"E111.0"),sQuery(id+"F3.wireOp",EDGE,"E112"),sQuery(id+"F3.wireOp",EDGE,"E113")])]});
            hole(context, id + "F21", {"style" : HoleStyle.SIMPLE, "endStyle" : HoleEndStyle.BLIND, "standardTappedOrClearance" : lookupTablePath({ "standard" : "ANSI", "fit" : "Close", "size" : "#8", "type" : "Clearance" }), "standardBlindInLast" : lookupTablePath({ "fit" : "Close", "standard" : "ANSI", "size" : "#8", "type" : "Clearance" }), "holeDiameter" : 4.32 * mm, "holeDepth" : 76.2 * mm, "isTappedThrough" : true, "tappedDepth" : 12.7 * mm, "tapClearance" : 3, "locations" : qUnion([Q0, Q1, Q2, Q3, Q4, Q5, Q6]), "scope" : qUnion([Q7, Q8, Q9])});
        }
        {
            var Q0;
            Q0=makeQuery(id+"F4.opExtrude","SWEPT_FACE",FACE,{"disambiguationData":[OSD([sQuery(id+"F3.wireOp",EDGE,"E78.MirrorCS")])]});
            var sketch = newSketch(context, id + "F22", { "sketchPlane" : qUnion([Q0])});
            skLineSegment(sketch, "E160", {"start": v(511.68, 273.05) * mm, "end": v(511.68, 146.05) * mm});
            skLineSegment(sketch, "E161", {"start": v(511.68, 209.55) * mm, "end": v(517.7, 209.55) * mm});
            skPoint(sketch, "E161.endSnap0", {"position": v(511.68, 209.55) * mm});
            skLineSegment(sketch, "E162", {"start": v(511.68, 209.55) * mm, "end": v(511.68, 234.95) * mm});
            skLineSegment(sketch, "E163", {"start": v(511.68, 234.95) * mm, "end": v(511.68, 260.35) * mm});
            skLineSegment(sketch, "E164.MirrorCS", {"start": v(511.68, 209.55) * mm, "end": v(511.68, 184.15) * mm});
            skLineSegment(sketch, "E165.MirrorCS", {"start": v(511.68, 184.15) * mm, "end": v(511.68, 158.75) * mm});
            skSolve(sketch);
        }
        {
            var Q0;
            Q0=sQuery(id+"F22.wireOp",VERTEX,"E163.end");
            var Q1;
            Q1=sQuery(id+"F22.wireOp",VERTEX,"E163.start");
            var Q2;
            Q2=sQuery(id+"F22.wireOp",VERTEX,"E161.endSnap0");
            var Q3;
            Q3=sQuery(id+"F22.wireOp",VERTEX,"E164.MirrorCS.end");
            var Q4;
            Q4=sQuery(id+"F22.wireOp",VERTEX,"E165.MirrorCS.end");
            var Q5;
            Q5=makeQuery(id+"F4.opExtrude","SWEPT_BODY",BODY,{"disambiguationData":[OSD([sQuery(id+"F3.wireOp",EDGE,"E14"),sQuery(id+"F3.wireOp",EDGE,"E17"),sQuery(id+"F3.wireOp",EDGE,"E20"),sQuery(id+"F3.wireOp",EDGE,"E22"),sQuery(id+"F3.wireOp",EDGE,"E31"),sQuery(id+"F3.wireOp",EDGE,"E32"),sQuery(id+"F3.wireOp",EDGE,"E33"),sQuery(id+"F3.wireOp",EDGE,"E34.trimOffspring"),sQuery(id+"F3.wireOp",EDGE,"E35.trimOffspring"),sQuery(id+"F3.wireOp",EDGE,"E44"),sQuery(id+"F3.wireOp",EDGE,"E45.filletArc"),sQuery(id+"F3.wireOp",EDGE,"E46.filletArc"),sQuery(id+"F3.wireOp",EDGE,"E47.filletArc"),sQuery(id+"F3.wireOp",EDGE,"E48.filletArc"),sQuery(id+"F3.wireOp",EDGE,"E55.filletArc"),sQuery(id+"F3.wireOp",EDGE,"E56.filletArc"),sQuery(id+"F3.wireOp",EDGE,"E59.MirrorCS"),sQuery(id+"F3.wireOp",EDGE,"E60.MirrorCS"),sQuery(id+"F3.wireOp",EDGE,"E61.MirrorCS"),sQuery(id+"F3.wireOp",EDGE,"E62.MirrorCS"),sQuery(id+"F3.wireOp",EDGE,"E63.MirrorCS"),sQuery(id+"F3.wireOp",EDGE,"E64.MirrorCS"),sQuery(id+"F3.wireOp",EDGE,"E65.MirrorCS"),sQuery(id+"F3.wireOp",EDGE,"E66.MirrorCS"),sQuery(id+"F3.wireOp",EDGE,"E75.MirrorCS"),sQuery(id+"F3.wireOp",EDGE,"E76.MirrorCS"),sQuery(id+"F3.wireOp",EDGE,"E77.MirrorCS"),sQuery(id+"F3.wireOp",EDGE,"E78.MirrorCS"),sQuery(id+"F3.wireOp",EDGE,"E79.MirrorCS"),sQuery(id+"F3.wireOp",EDGE,"E114.trimOffspring"),sQuery(id+"F3.wireOp",EDGE,"E115.trimOffspring"),sQuery(id+"F3.wireOp",EDGE,"E116.trimOffspring"),sQuery(id+"F3.wireOp",EDGE,"E117.filletArc"),sQuery(id+"F3.wireOp",EDGE,"E118.filletArc")])]});
            var Q6;
            Q6=makeQuery(id+"F7.opExtrude","SWEPT_BODY",BODY,{"disambiguationData":[OSD([sQuery(id+"F3.wireOp",EDGE,"E42")])]});
            var Q7;
            Q7=makeQuery(id+"F7.opExtrude","SWEPT_BODY",BODY,{"disambiguationData":[OSD([sQuery(id+"F3.wireOp",EDGE,"E90.MirrorCS")])]});
            hole(context, id + "F23", {"style" : HoleStyle.SIMPLE, "endStyle" : HoleEndStyle.BLIND, "standardTappedOrClearance" : lookupTablePath({ "standard" : "ANSI", "fit" : "Close", "size" : "#8", "type" : "Clearance" }), "standardBlindInLast" : lookupTablePath({ "fit" : "Close", "standard" : "ANSI", "size" : "#8", "type" : "Clearance" }), "holeDiameter" : 4.32 * mm, "holeDepth" : 76.2 * mm, "isTappedThrough" : true, "tappedDepth" : 12.7 * mm, "tapClearance" : 3, "locations" : qUnion([Q0, Q1, Q2, Q3, Q4]), "scope" : qUnion([Q5, Q6, Q7])});
        }
        {
            var Q0;
            Q0=makeQuery(id+"F4.opExtrude","SWEPT_FACE",FACE,{"disambiguationData":[OSD([sQuery(id+"F3.wireOp",EDGE,"E103.MirrorCS")])]});
            var sketch = newSketch(context, id + "F24", { "sketchPlane" : qUnion([Q0])});
            skLineSegment(sketch, "E166", {"start": v(196.17, 273.05) * mm, "end": v(196.17, 146.05) * mm});
            skLineSegment(sketch, "E167", {"start": v(196.17, 146.05) * mm, "end": v(196.17, 184.15) * mm});
            skLineSegment(sketch, "E168", {"start": v(196.17, 184.15) * mm, "end": v(196.17, 222.25) * mm});
            skLineSegment(sketch, "E169", {"start": v(196.17, 222.25) * mm, "end": v(196.17, 260.35) * mm});
            skLineSegment(sketch, "E170", {"start": v(196.17, 146.05) * mm, "end": v(135.22, 146.05) * mm});
            skLineSegment(sketch, "E171.MirrorCS", {"start": v(196.17, 19.05) * mm, "end": v(196.17, 146.05) * mm});
            skLineSegment(sketch, "E172.MirrorCS", {"start": v(196.17, 146.05) * mm, "end": v(196.17, 107.95) * mm});
            skLineSegment(sketch, "E173.MirrorCS", {"start": v(196.17, 107.95) * mm, "end": v(196.17, 69.85) * mm});
            skLineSegment(sketch, "E174.MirrorCS", {"start": v(196.17, 69.85) * mm, "end": v(196.17, 31.75) * mm});
            skSolve(sketch);
        }
        {
            var Q0;
            Q0=makeQuery(id+"F4.opExtrude","SWEPT_FACE",FACE,{"disambiguationData":[OSD([sQuery(id+"F3.wireOp",EDGE,"E40")])]});
            var sketch = newSketch(context, id + "F25", { "sketchPlane" : qUnion([Q0])});
            skLineSegment(sketch, "E175", {"start": v(-196.17, 273.05) * mm, "end": v(-196.17, 146.05) * mm});
            skLineSegment(sketch, "E176", {"start": v(-196.17, 146.05) * mm, "end": v(-152.27, 146.05) * mm});
            skLineSegment(sketch, "E177", {"start": v(-196.17, 146.05) * mm, "end": v(-196.17, 184.15) * mm});
            skLineSegment(sketch, "E178", {"start": v(-196.17, 184.15) * mm, "end": v(-196.17, 222.25) * mm});
            skLineSegment(sketch, "E179", {"start": v(-196.17, 222.25) * mm, "end": v(-196.17, 260.35) * mm});
            skLineSegment(sketch, "E180.MirrorCS", {"start": v(-196.17, 146.05) * mm, "end": v(-196.17, 107.95) * mm});
            skLineSegment(sketch, "E181.MirrorCS", {"start": v(-196.17, 69.85) * mm, "end": v(-196.17, 31.75) * mm});
            skLineSegment(sketch, "E182.MirrorCS", {"start": v(-196.17, 107.95) * mm, "end": v(-196.17, 69.85) * mm});
            skLineSegment(sketch, "E183.MirrorCS", {"start": v(-196.17, 19.05) * mm, "end": v(-196.17, 146.05) * mm});
            skSolve(sketch);
        }
        {
            var Q0;
            Q0=sQuery(id+"F25.wireOp",VERTEX,"E179.end");
            var Q1;
            Q1=sQuery(id+"F25.wireOp",VERTEX,"E178.end");
            var Q2;
            Q2=sQuery(id+"F25.wireOp",VERTEX,"E177.end");
            var Q3;
            Q3=sQuery(id+"F25.wireOp",VERTEX,"E177.start");
            var Q4;
            Q4=sQuery(id+"F25.wireOp",VERTEX,"E182.MirrorCS.start");
            var Q5;
            Q5=sQuery(id+"F25.wireOp",VERTEX,"E182.MirrorCS.end");
            var Q6;
            Q6=sQuery(id+"F25.wireOp",VERTEX,"E181.MirrorCS.end");
            var Q7;
            Q7=makeQuery(id+"F4.opExtrude","SWEPT_BODY",BODY,{"disambiguationData":[OSD([sQuery(id+"F3.wireOp",EDGE,"E24"),sQuery(id+"F3.wireOp",EDGE,"E26"),sQuery(id+"F3.wireOp",EDGE,"E27"),sQuery(id+"F3.wireOp",EDGE,"E37"),sQuery(id+"F3.wireOp",EDGE,"E38.trimOffspring"),sQuery(id+"F3.wireOp",EDGE,"E39.trimOffspring"),sQuery(id+"F3.wireOp",EDGE,"E40"),sQuery(id+"F3.wireOp",EDGE,"E41"),sQuery(id+"F3.wireOp",EDGE,"E42"),sQuery(id+"F3.wireOp",EDGE,"E43.trimOffspring"),sQuery(id+"F3.wireOp",EDGE,"E49.filletArc"),sQuery(id+"F3.wireOp",EDGE,"E50.filletArc"),sQuery(id+"F3.wireOp",EDGE,"E51.filletArc"),sQuery(id+"F3.wireOp",EDGE,"E52.filletArc"),sQuery(id+"F3.wireOp",EDGE,"E53.trimOffspring"),sQuery(id+"F3.wireOp",EDGE,"E54.trimOffspring"),sQuery(id+"F3.wireOp",EDGE,"E57.filletArc"),sQuery(id+"F3.wireOp",EDGE,"E58.filletArc"),sQuery(id+"F3.wireOp",EDGE,"E81.MirrorCS"),sQuery(id+"F3.wireOp",EDGE,"E82.MirrorCS"),sQuery(id+"F3.wireOp",EDGE,"E83.MirrorCS"),sQuery(id+"F3.wireOp",EDGE,"E84.MirrorCS"),sQuery(id+"F3.wireOp",EDGE,"E85.MirrorCS"),sQuery(id+"F3.wireOp",EDGE,"E86.MirrorCS"),sQuery(id+"F3.wireOp",EDGE,"E87.MirrorCS"),sQuery(id+"F3.wireOp",EDGE,"E88.MirrorCS"),sQuery(id+"F3.wireOp",EDGE,"E89.MirrorCS"),sQuery(id+"F3.wireOp",EDGE,"E90.MirrorCS"),sQuery(id+"F3.wireOp",EDGE,"E91.MirrorCS"),sQuery(id+"F3.wireOp",EDGE,"E93.MirrorCS"),sQuery(id+"F3.wireOp",EDGE,"E97.MirrorCS"),sQuery(id+"F3.wireOp",EDGE,"E99.MirrorCS"),sQuery(id+"F3.wireOp",EDGE,"E101.MirrorCS"),sQuery(id+"F3.wireOp",EDGE,"E103.MirrorCS"),sQuery(id+"F3.wireOp",EDGE,"E104.MirrorCS"),sQuery(id+"F3.wireOp",EDGE,"E105.MirrorCS"),sQuery(id+"F3.wireOp",EDGE,"E106"),sQuery(id+"F3.wireOp",EDGE,"E107"),sQuery(id+"F3.wireOp",EDGE,"E109.filletArc"),sQuery(id+"F3.wireOp",EDGE,"E110.0"),sQuery(id+"F3.wireOp",EDGE,"E111.0"),sQuery(id+"F3.wireOp",EDGE,"E112"),sQuery(id+"F3.wireOp",EDGE,"E113")])]});
            var Q8;
            Q8=makeQuery(id+"F2.opExtrude","SWEPT_BODY",BODY,{"disambiguationData":[OSD([sQuery(id+"F0.wireOp",EDGE,"E0.bottom"),sQuery(id+"F0.wireOp",EDGE,"E0.top"),sQuery(id+"F0.wireOp",EDGE,"E0.left"),sQuery(id+"F0.wireOp",EDGE,"E0.right"),sQuery(id+"F0.wireOp",EDGE,"E7"),sQuery(id+"F0.wireOp",EDGE,"E8"),sQuery(id+"F0.wireOp",EDGE,"E9"),sQuery(id+"F0.wireOp",EDGE,"E10"),sQuery(id+"F0.wireOp",EDGE,"E11.1.0"),sQuery(id+"F0.wireOp",EDGE,"E11.1.1"),sQuery(id+"F0.wireOp",EDGE,"E11.1.2"),sQuery(id+"F0.wireOp",EDGE,"E11.1.3"),sQuery(id+"F0.wireOp",EDGE,"E11.1.4"),sQuery(id+"F0.wireOp",EDGE,"E11.2.0"),sQuery(id+"F0.wireOp",EDGE,"E11.2.1"),sQuery(id+"F0.wireOp",EDGE,"E11.2.2"),sQuery(id+"F0.wireOp",EDGE,"E11.2.3"),sQuery(id+"F0.wireOp",EDGE,"E11.2.4"),sQuery(id+"F0.wireOp",EDGE,"E11.3.0"),sQuery(id+"F0.wireOp",EDGE,"E11.3.1"),sQuery(id+"F0.wireOp",EDGE,"E11.3.2"),sQuery(id+"F0.wireOp",EDGE,"E11.3.3"),sQuery(id+"F0.wireOp",EDGE,"E11.3.4"),sQuery(id+"F0.wireOp",EDGE,"E12.0"),sQuery(id+"F0.wireOp",EDGE,"E12.1"),sQuery(id+"F0.wireOp",EDGE,"E12.2"),sQuery(id+"F0.wireOp",EDGE,"E12.3")])]});
            hole(context, id + "F26", {"style" : HoleStyle.SIMPLE, "endStyle" : HoleEndStyle.BLIND, "standardTappedOrClearance" : lookupTablePath({ "standard" : "ANSI", "fit" : "Close", "size" : "#8", "type" : "Clearance" }), "standardBlindInLast" : lookupTablePath({ "fit" : "Close", "standard" : "ANSI", "size" : "#8", "type" : "Clearance" }), "holeDiameter" : 4.32 * mm, "holeDepth" : 76.2 * mm, "isTappedThrough" : true, "tappedDepth" : 12.7 * mm, "tapClearance" : 3, "locations" : qUnion([Q0, Q1, Q2, Q3, Q4, Q5, Q6]), "scope" : qUnion([Q7, Q8])});
        }
        {
            var Q0;
            Q0=sQuery(id+"F24.wireOp",VERTEX,"E169.end");
            var Q1;
            Q1=sQuery(id+"F24.wireOp",VERTEX,"E169.start");
            var Q2;
            Q2=sQuery(id+"F24.wireOp",VERTEX,"E168.start");
            var Q3;
            Q3=sQuery(id+"F24.wireOp",VERTEX,"E166.end");
            var Q4;
            Q4=sQuery(id+"F24.wireOp",VERTEX,"E172.MirrorCS.end");
            var Q5;
            Q5=sQuery(id+"F24.wireOp",VERTEX,"E173.MirrorCS.end");
            var Q6;
            Q6=sQuery(id+"F24.wireOp",VERTEX,"E174.MirrorCS.end");
            var Q7;
            Q7=makeQuery(id+"F4.opExtrude","SWEPT_BODY",BODY,{"disambiguationData":[OSD([sQuery(id+"F3.wireOp",EDGE,"E24"),sQuery(id+"F3.wireOp",EDGE,"E26"),sQuery(id+"F3.wireOp",EDGE,"E27"),sQuery(id+"F3.wireOp",EDGE,"E37"),sQuery(id+"F3.wireOp",EDGE,"E38.trimOffspring"),sQuery(id+"F3.wireOp",EDGE,"E39.trimOffspring"),sQuery(id+"F3.wireOp",EDGE,"E40"),sQuery(id+"F3.wireOp",EDGE,"E41"),sQuery(id+"F3.wireOp",EDGE,"E42"),sQuery(id+"F3.wireOp",EDGE,"E43.trimOffspring"),sQuery(id+"F3.wireOp",EDGE,"E49.filletArc"),sQuery(id+"F3.wireOp",EDGE,"E50.filletArc"),sQuery(id+"F3.wireOp",EDGE,"E51.filletArc"),sQuery(id+"F3.wireOp",EDGE,"E52.filletArc"),sQuery(id+"F3.wireOp",EDGE,"E53.trimOffspring"),sQuery(id+"F3.wireOp",EDGE,"E54.trimOffspring"),sQuery(id+"F3.wireOp",EDGE,"E57.filletArc"),sQuery(id+"F3.wireOp",EDGE,"E58.filletArc"),sQuery(id+"F3.wireOp",EDGE,"E81.MirrorCS"),sQuery(id+"F3.wireOp",EDGE,"E82.MirrorCS"),sQuery(id+"F3.wireOp",EDGE,"E83.MirrorCS"),sQuery(id+"F3.wireOp",EDGE,"E84.MirrorCS"),sQuery(id+"F3.wireOp",EDGE,"E85.MirrorCS"),sQuery(id+"F3.wireOp",EDGE,"E86.MirrorCS"),sQuery(id+"F3.wireOp",EDGE,"E87.MirrorCS"),sQuery(id+"F3.wireOp",EDGE,"E88.MirrorCS"),sQuery(id+"F3.wireOp",EDGE,"E89.MirrorCS"),sQuery(id+"F3.wireOp",EDGE,"E90.MirrorCS"),sQuery(id+"F3.wireOp",EDGE,"E91.MirrorCS"),sQuery(id+"F3.wireOp",EDGE,"E93.MirrorCS"),sQuery(id+"F3.wireOp",EDGE,"E97.MirrorCS"),sQuery(id+"F3.wireOp",EDGE,"E99.MirrorCS"),sQuery(id+"F3.wireOp",EDGE,"E101.MirrorCS"),sQuery(id+"F3.wireOp",EDGE,"E103.MirrorCS"),sQuery(id+"F3.wireOp",EDGE,"E104.MirrorCS"),sQuery(id+"F3.wireOp",EDGE,"E105.MirrorCS"),sQuery(id+"F3.wireOp",EDGE,"E106"),sQuery(id+"F3.wireOp",EDGE,"E107"),sQuery(id+"F3.wireOp",EDGE,"E109.filletArc"),sQuery(id+"F3.wireOp",EDGE,"E110.0"),sQuery(id+"F3.wireOp",EDGE,"E111.0"),sQuery(id+"F3.wireOp",EDGE,"E112"),sQuery(id+"F3.wireOp",EDGE,"E113")])]});
            var Q8;
            Q8=makeQuery(id+"F2.opExtrude","SWEPT_BODY",BODY,{"disambiguationData":[OSD([sQuery(id+"F0.wireOp",EDGE,"E0.bottom"),sQuery(id+"F0.wireOp",EDGE,"E0.top"),sQuery(id+"F0.wireOp",EDGE,"E0.left"),sQuery(id+"F0.wireOp",EDGE,"E0.right"),sQuery(id+"F0.wireOp",EDGE,"E7"),sQuery(id+"F0.wireOp",EDGE,"E8"),sQuery(id+"F0.wireOp",EDGE,"E9"),sQuery(id+"F0.wireOp",EDGE,"E10"),sQuery(id+"F0.wireOp",EDGE,"E11.1.0"),sQuery(id+"F0.wireOp",EDGE,"E11.1.1"),sQuery(id+"F0.wireOp",EDGE,"E11.1.2"),sQuery(id+"F0.wireOp",EDGE,"E11.1.3"),sQuery(id+"F0.wireOp",EDGE,"E11.1.4"),sQuery(id+"F0.wireOp",EDGE,"E11.2.0"),sQuery(id+"F0.wireOp",EDGE,"E11.2.1"),sQuery(id+"F0.wireOp",EDGE,"E11.2.2"),sQuery(id+"F0.wireOp",EDGE,"E11.2.3"),sQuery(id+"F0.wireOp",EDGE,"E11.2.4"),sQuery(id+"F0.wireOp",EDGE,"E11.3.0"),sQuery(id+"F0.wireOp",EDGE,"E11.3.1"),sQuery(id+"F0.wireOp",EDGE,"E11.3.2"),sQuery(id+"F0.wireOp",EDGE,"E11.3.3"),sQuery(id+"F0.wireOp",EDGE,"E11.3.4"),sQuery(id+"F0.wireOp",EDGE,"E12.0"),sQuery(id+"F0.wireOp",EDGE,"E12.1"),sQuery(id+"F0.wireOp",EDGE,"E12.2"),sQuery(id+"F0.wireOp",EDGE,"E12.3")])]});
            hole(context, id + "F27", {"style" : HoleStyle.SIMPLE, "endStyle" : HoleEndStyle.BLIND, "standardTappedOrClearance" : lookupTablePath({ "standard" : "ANSI", "fit" : "Close", "size" : "#8", "type" : "Clearance" }), "standardBlindInLast" : lookupTablePath({ "fit" : "Close", "standard" : "ANSI", "size" : "#8", "type" : "Clearance" }), "holeDiameter" : 4.32 * mm, "holeDepth" : 76.2 * mm, "isTappedThrough" : true, "tappedDepth" : 12.7 * mm, "tapClearance" : 3, "locations" : qUnion([Q0, Q1, Q2, Q3, Q4, Q5, Q6]), "scope" : qUnion([Q7, Q8])});
        }
    });
